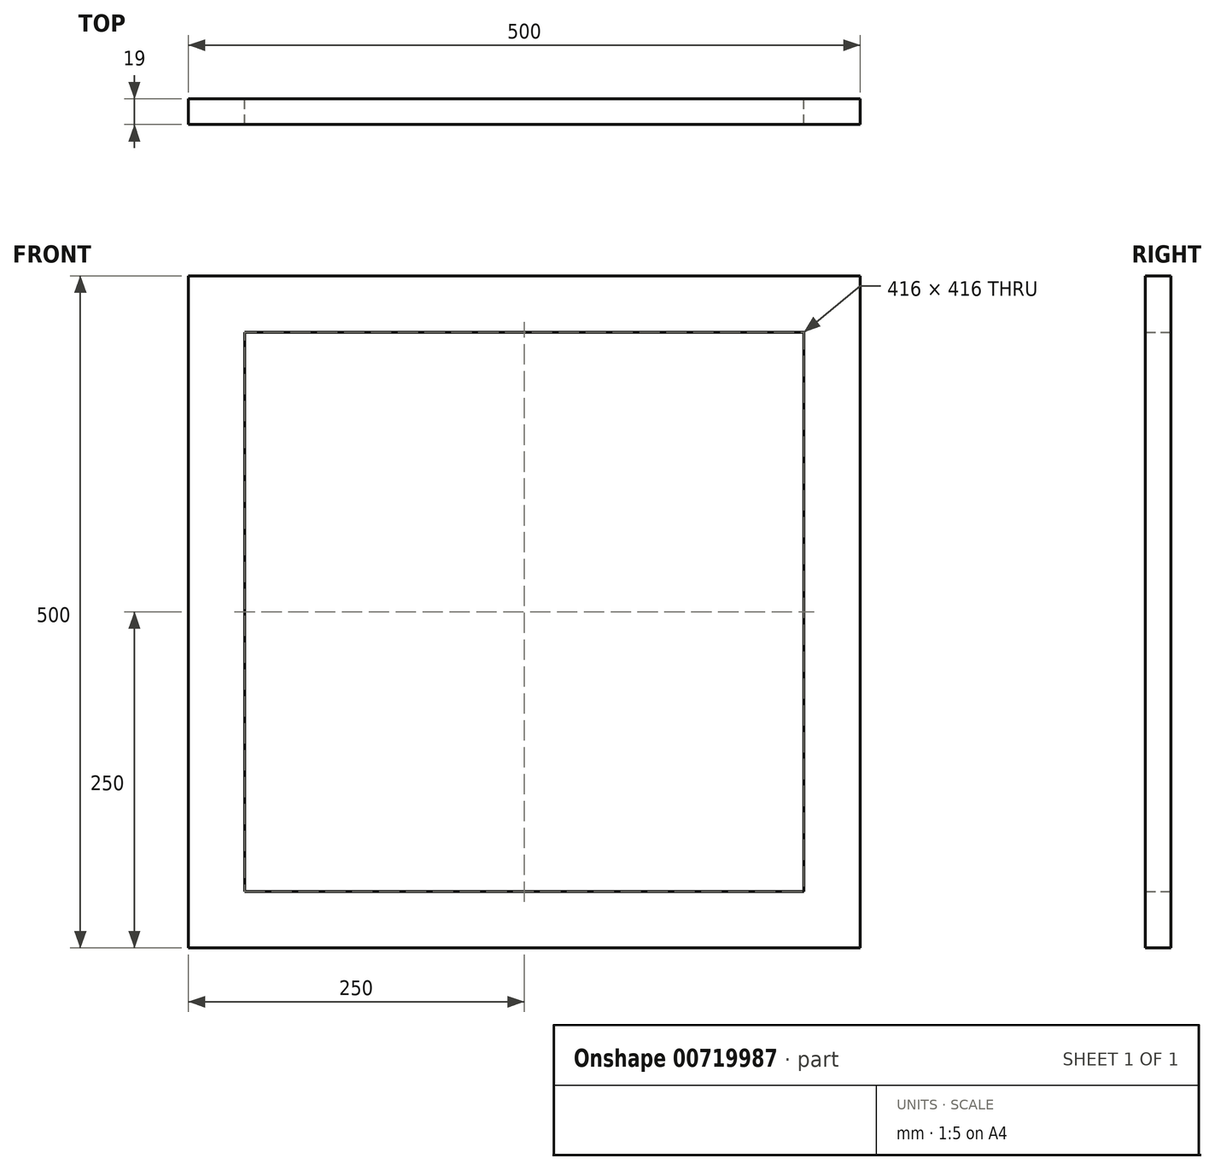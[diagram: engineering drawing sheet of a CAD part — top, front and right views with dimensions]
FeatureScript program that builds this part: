
annotation { "Feature Type Name" : "Feature", "Feature Type Description" : "" }
export const myFeature = defineFeature(function(context is Context, id is Id, definition is map)
    precondition{}
    {
        {
            var Q0;
            Q0=qCreatedBy(makeId("Front.planeOp"),FACE);
            var sketch = newSketch(context, id + "F0", { "sketchPlane" : qUnion([Q0])});
            skLineSegment(sketch, "E0.bottom", {"start": v(208, -21) * mm, "end": v(-208, -21) * mm});
            skLineSegment(sketch, "E0.top", {"start": v(208, 21) * mm, "end": v(-208, 21) * mm});
            skLineSegment(sketch, "E0.left", {"start": v(208, -21) * mm, "end": v(208, 21) * mm});
            skLineSegment(sketch, "E0.right", {"start": v(-208, -21) * mm, "end": v(-208, 21) * mm});
            skPoint(sketch, "E0.middle", {"position": v(0, 0) * mm});
            skLineSegment(sketch, "E1.bottom", {"start": v(-208, 21) * mm, "end": v(-250, 21) * mm});
            skLineSegment(sketch, "E1.top", {"start": v(-208, -479) * mm, "end": v(-250, -479) * mm});
            skLineSegment(sketch, "E1.left", {"start": v(-208, 21) * mm, "end": v(-208, -479) * mm});
            skLineSegment(sketch, "E1.right", {"start": v(-250, 21) * mm, "end": v(-250, -479) * mm});
            skLineSegment(sketch, "E2.bottom", {"start": v(-208, -479) * mm, "end": v(208, -479) * mm});
            skLineSegment(sketch, "E2.top", {"start": v(-208, -437) * mm, "end": v(208, -437) * mm});
            skLineSegment(sketch, "E2.left", {"start": v(-208, -479) * mm, "end": v(-208, -437) * mm});
            skLineSegment(sketch, "E2.right", {"start": v(208, -479) * mm, "end": v(208, -437) * mm});
            skLineSegment(sketch, "E3.bottom", {"start": v(208, -479) * mm, "end": v(250, -479) * mm});
            skLineSegment(sketch, "E3.top", {"start": v(208, 21) * mm, "end": v(250, 21) * mm});
            skLineSegment(sketch, "E3.left", {"start": v(208, -479) * mm, "end": v(208, 21) * mm});
            skLineSegment(sketch, "E3.right", {"start": v(250, -479) * mm, "end": v(250, 21) * mm});
            skLineSegment(sketch, "E4.bottom", {"start": v(-250, 21) * mm, "end": v(-208, 21) * mm});
            skLineSegment(sketch, "E5.bottom", {"start": v(250, 21) * mm, "end": v(208, 21) * mm});
            skPoint(sketch, "E5.top.end.orphan", {"position": v(208, 40) * mm});
            skSolve(sketch);
        }
        {
            var Q0;
            Q0 = qSketchRegion(id + "F0", true);
            extrude(context, id + "F1", {"entities" : qUnion([Q0]), "depth" : 19 * mm, "offsetDistance" : 25 * mm});
        }
    });
